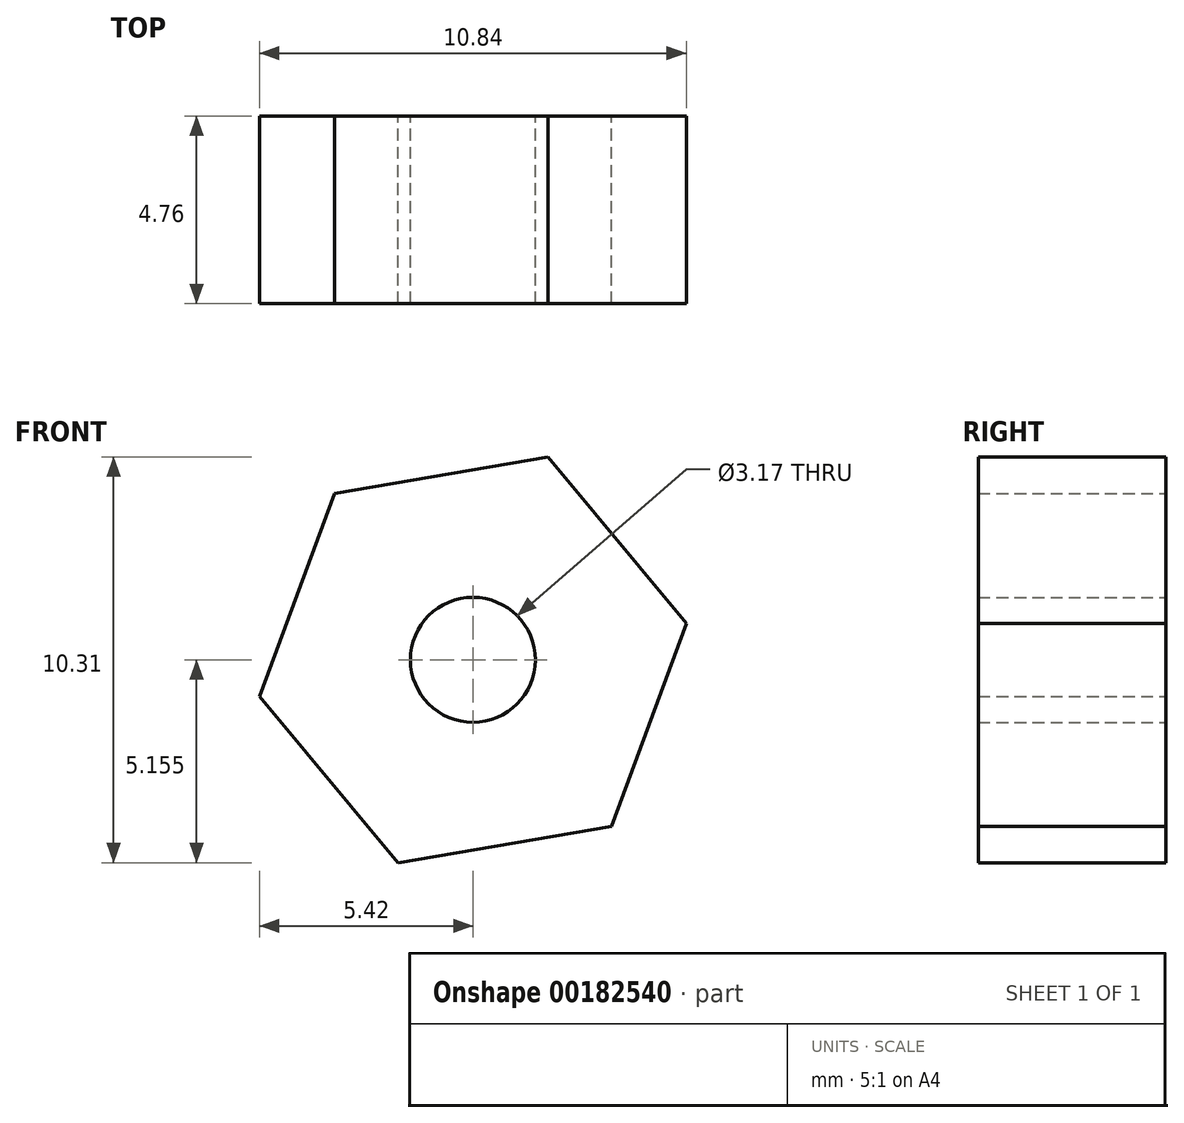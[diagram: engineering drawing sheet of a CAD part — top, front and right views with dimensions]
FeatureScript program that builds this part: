
annotation { "Feature Type Name" : "Feature", "Feature Type Description" : "" }
export const myFeature = defineFeature(function(context is Context, id is Id, definition is map)
    precondition{}
    {
        {
            var Q0;
            Q0=qCreatedBy(makeId("Front.planeOp"),FACE);
            var sketch = newSketch(context, id + "F0", { "sketchPlane" : qUnion([Q0])});
            skCircle(sketch, "E0", {"center": v(-35.5, 37.73) * mm, "radius": 1.59 * mm});
            skCircle(sketch, "E1.cCircle", {"center": v(-35.5, 37.73) * mm, "radius": 5.5 * mm, "construction": true});
            skLineSegment(sketch, "E1.0", {"start": v(-39, 41.96) * mm, "end": v(-33.58, 42.88) * mm});
            skLineSegment(sketch, "E1.1", {"start": v(-33.58, 42.88) * mm, "end": v(-30.07, 38.65) * mm});
            skLineSegment(sketch, "E1.2", {"start": v(-30.07, 38.65) * mm, "end": v(-31.98, 33.5) * mm});
            skLineSegment(sketch, "E1.3", {"start": v(-31.98, 33.5) * mm, "end": v(-37.4, 32.57) * mm});
            skLineSegment(sketch, "E1.4", {"start": v(-37.4, 32.57) * mm, "end": v(-40.91, 36.8) * mm});
            skLineSegment(sketch, "E1.5", {"start": v(-40.91, 36.8) * mm, "end": v(-39, 41.96) * mm});
            skSolve(sketch);
        }
        {
            var Q0;
            Q0 = qSketchRegion(id + "F0", true);
            extrude(context, id + "F1", {"entities" : qUnion([Q0]), "depth" : 4.76 * mm});
        }
    });
